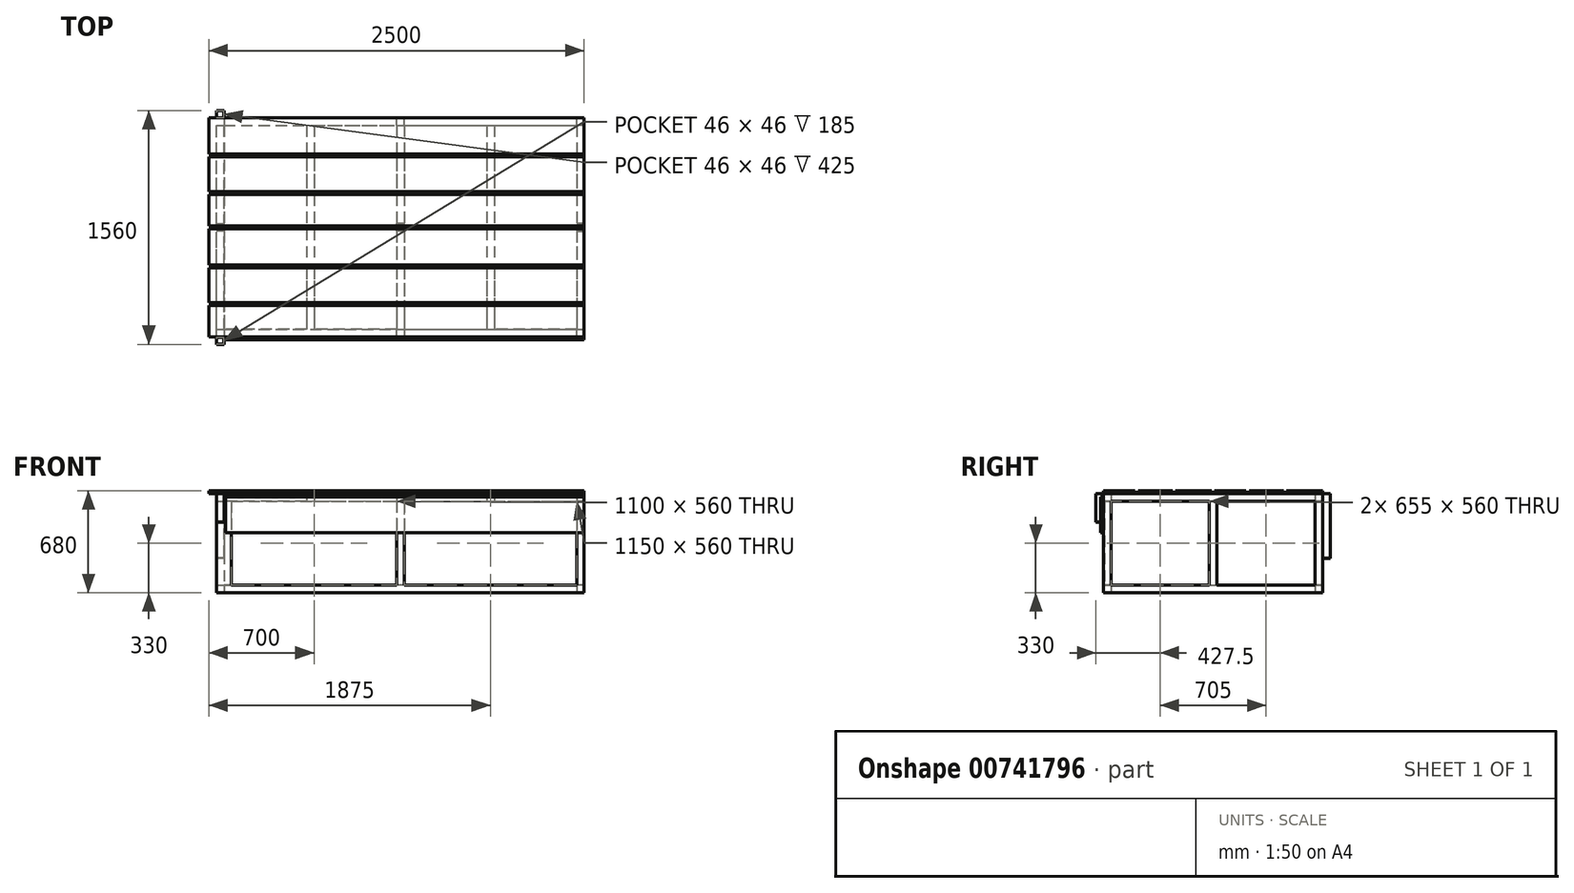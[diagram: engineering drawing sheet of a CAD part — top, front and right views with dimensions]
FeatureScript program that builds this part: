
annotation { "Feature Type Name" : "Feature", "Feature Type Description" : "" }
export const myFeature = defineFeature(function(context is Context, id is Id, definition is map)
    precondition{}
    {
        {
            var Q0;
            Q0=qCreatedBy(makeId("Top.planeOp"),FACE);
            var sketch = newSketch(context, id + "F0", { "sketchPlane" : qUnion([Q0])});
            skLineSegment(sketch, "E0.bottom", {"start": v(1225, -730) * mm, "end": v(-1225, -730) * mm});
            skLineSegment(sketch, "E0.top", {"start": v(1225, 730) * mm, "end": v(-1225, 730) * mm});
            skLineSegment(sketch, "E0.left", {"start": v(1225, -730) * mm, "end": v(1225, 730) * mm});
            skLineSegment(sketch, "E0.right", {"start": v(-1225, -730) * mm, "end": v(-1225, 730) * mm});
            skPoint(sketch, "E0.middle", {"position": v(0, 0) * mm});
            skLineSegment(sketch, "E1.bottom", {"start": v(-1175, 680) * mm, "end": v(1175, 680) * mm});
            skLineSegment(sketch, "E1.top", {"start": v(-1175, -680) * mm, "end": v(1175, -680) * mm});
            skLineSegment(sketch, "E1.left", {"start": v(-1175, 680) * mm, "end": v(-1175, -680) * mm});
            skLineSegment(sketch, "E1.right", {"start": v(1175, 680) * mm, "end": v(1175, -680) * mm});
            skLineSegment(sketch, "E2.bottom", {"start": v(25, 680) * mm, "end": v(-25, 680) * mm});
            skLineSegment(sketch, "E2.top", {"start": v(25, -680) * mm, "end": v(-25, -680) * mm});
            skLineSegment(sketch, "E2.left", {"start": v(25, 680) * mm, "end": v(25, -680) * mm});
            skLineSegment(sketch, "E2.right", {"start": v(-25, 680) * mm, "end": v(-25, -680) * mm});
            skSolve(sketch);
        }
        {
            var Q0;
            Q0 = qSketchRegion(id + "F0", true);
            var Q1;
            Q1=makeQuery(id+"F0.imprint","IMPRINT",FACE,{"disambiguationData":[TD([[makeQuery(id+"F0.imprint","IMPRINT",EDGE,{"derivedFrom":sQuery(id+"F0.wireOp",EDGE,"E2.bottom")}),1.0]])]});
            extrude(context, id + "F1", {"entities" : qUnion([Q0, Q1]), "depth" : 50 * mm, "offsetDistance" : 25 * mm});
        }
        {
            var Q0;
            Q0=makeQuery(id+"F1.opExtrude","CAP_FACE",FACE,{"disambiguationData":[OSD([sQuery(id+"F0.wireOp",EDGE,"E0.bottom"),sQuery(id+"F0.wireOp",EDGE,"E0.top"),sQuery(id+"F0.wireOp",EDGE,"E0.left"),sQuery(id+"F0.wireOp",EDGE,"E0.right"),sQuery(id+"F0.wireOp",EDGE,"E1.bottom"),sQuery(id+"F0.wireOp",EDGE,"E1.top"),sQuery(id+"F0.wireOp",EDGE,"E1.left"),sQuery(id+"F0.wireOp",EDGE,"E1.right"),sQuery(id+"F0.wireOp",EDGE,"E2.left"),sQuery(id+"F0.wireOp",EDGE,"E2.right")])],"isStart":false});
            var sketch = newSketch(context, id + "F2", { "sketchPlane" : qUnion([Q0])});
            skLineSegment(sketch, "E3.bottom", {"start": v(-1225, 730) * mm, "end": v(-1175, 730) * mm});
            skLineSegment(sketch, "E3.top", {"start": v(-1225, 680) * mm, "end": v(-1175, 680) * mm});
            skLineSegment(sketch, "E3.left", {"start": v(-1225, 730) * mm, "end": v(-1225, 680) * mm});
            skLineSegment(sketch, "E3.right", {"start": v(-1175, 730) * mm, "end": v(-1175, 680) * mm});
            skLineSegment(sketch, "E4", {"start": v(-25, 680) * mm, "end": v(-25, 730) * mm});
            skLineSegment(sketch, "E5", {"start": v(25, 680) * mm, "end": v(25, 730) * mm});
            skLineSegment(sketch, "E6", {"start": v(25, 730) * mm, "end": v(-25, 730) * mm});
            skLineSegment(sketch, "E7", {"start": v(-25, 680) * mm, "end": v(25, 680) * mm});
            skLineSegment(sketch, "E8", {"start": v(1175, 680) * mm, "end": v(1175, 730) * mm});
            skLineSegment(sketch, "E9", {"start": v(1175, 730) * mm, "end": v(1225, 730) * mm});
            skLineSegment(sketch, "E10", {"start": v(1225, 730) * mm, "end": v(1225, 680) * mm});
            skLineSegment(sketch, "E11", {"start": v(1225, 680) * mm, "end": v(1175, 680) * mm});
            skLineSegment(sketch, "E12", {"start": v(1175, -680) * mm, "end": v(1225, -680) * mm});
            skLineSegment(sketch, "E13", {"start": v(1225, -680) * mm, "end": v(1225, -730) * mm});
            skLineSegment(sketch, "E14", {"start": v(1225, -730) * mm, "end": v(1175, -730) * mm});
            skLineSegment(sketch, "E15", {"start": v(1175, -730) * mm, "end": v(1175, -680) * mm});
            skLineSegment(sketch, "E16", {"start": v(-25, -680) * mm, "end": v(25, -680) * mm});
            skLineSegment(sketch, "E17", {"start": v(25, -680) * mm, "end": v(25, -730) * mm});
            skLineSegment(sketch, "E18", {"start": v(25, -730) * mm, "end": v(-25, -730) * mm});
            skLineSegment(sketch, "E19", {"start": v(-25, -730) * mm, "end": v(-25, -680) * mm});
            skLineSegment(sketch, "E20", {"start": v(-1175, -680) * mm, "end": v(-1175, -730) * mm});
            skLineSegment(sketch, "E21", {"start": v(-1175, -730) * mm, "end": v(-1225, -730) * mm});
            skLineSegment(sketch, "E22", {"start": v(-1225, -730) * mm, "end": v(-1225, -680) * mm});
            skLineSegment(sketch, "E23", {"start": v(-1225, -680) * mm, "end": v(-1175, -680) * mm});
            skLineSegment(sketch, "E24.bottom", {"start": v(25, -25) * mm, "end": v(-25, -25) * mm});
            skLineSegment(sketch, "E24.top", {"start": v(25, 25) * mm, "end": v(-25, 25) * mm});
            skLineSegment(sketch, "E24.left", {"start": v(25, -25) * mm, "end": v(25, 25) * mm});
            skLineSegment(sketch, "E24.right", {"start": v(-25, -25) * mm, "end": v(-25, 25) * mm});
            skPoint(sketch, "E24.middle", {"position": v(0, 0) * mm});
            skLineSegment(sketch, "E25", {"start": v(0, 0) * mm, "end": v(-1225, 0) * mm});
            skLineSegment(sketch, "E26", {"start": v(-1225, 25) * mm, "end": v(-1175, 25) * mm});
            skLineSegment(sketch, "E27", {"start": v(-1175, 25) * mm, "end": v(-1175, -25) * mm});
            skLineSegment(sketch, "E28", {"start": v(-1175, -25) * mm, "end": v(-1225, -25) * mm});
            skLineSegment(sketch, "E29", {"start": v(-1225, 25) * mm, "end": v(-1225, -25) * mm});
            skLineSegment(sketch, "E30.MirrorCS", {"start": v(1225, 25) * mm, "end": v(1225, -25) * mm});
            skLineSegment(sketch, "E31.MirrorCS", {"start": v(1175, -25) * mm, "end": v(1225, -25) * mm});
            skLineSegment(sketch, "E32.MirrorCS", {"start": v(1225, 25) * mm, "end": v(1175, 25) * mm});
            skLineSegment(sketch, "E33.MirrorCS", {"start": v(1175, 25) * mm, "end": v(1175, -25) * mm});
            skSolve(sketch);
        }
        {
            var Q0;
            Q0 = qSketchRegion(id + "F2", true);
            extrude(context, id + "F3", {"entities" : qUnion([Q0]), "operationType" : NewBodyOperationType.ADD, "depth" : 560 * mm, "offsetDistance" : 25 * mm});
        }
        {
            var Q0;
            Q0=makeQuery(id+"F3.opExtrude","CAP_FACE",FACE,{"disambiguationData":[OSD([sQuery(id+"F2.wireOp",EDGE,"E26"),sQuery(id+"F2.wireOp",EDGE,"E27"),sQuery(id+"F2.wireOp",EDGE,"E28"),sQuery(id+"F2.wireOp",EDGE,"E29")])],"isStart":false});
            var sketch = newSketch(context, id + "F4", { "sketchPlane" : qUnion([Q0])});
            skLineSegment(sketch, "E34", {"start": v(-1225, 25) * mm, "end": v(-1225, 730) * mm});
            skLineSegment(sketch, "E35", {"start": v(-1225, 730) * mm, "end": v(-1175, 730) * mm});
            skLineSegment(sketch, "E36", {"start": v(-1175, 730) * mm, "end": v(1225, 730) * mm});
            skLineSegment(sketch, "E37", {"start": v(1225, 730) * mm, "end": v(1225, -730) * mm});
            skLineSegment(sketch, "E38", {"start": v(1225, -730) * mm, "end": v(-1225, -730) * mm});
            skLineSegment(sketch, "E39", {"start": v(-1225, -730) * mm, "end": v(-1225, 25) * mm});
            skLineSegment(sketch, "E40", {"start": v(-1175, 730) * mm, "end": v(-1175, 680) * mm});
            skLineSegment(sketch, "E41", {"start": v(-1175, 680) * mm, "end": v(-25, 680) * mm});
            skLineSegment(sketch, "E42", {"start": v(-1175, 680) * mm, "end": v(-600, 680) * mm});
            skLineSegment(sketch, "E43", {"start": v(-600, 680) * mm, "end": v(-575, 680) * mm});
            skLineSegment(sketch, "E44", {"start": v(-600, 680) * mm, "end": v(-625, 680) * mm});
            skLineSegment(sketch, "E45", {"start": v(-625, 680) * mm, "end": v(-625, -680) * mm});
            skLineSegment(sketch, "E46.MirrorCS", {"start": v(-575, 680) * mm, "end": v(-575, -680) * mm});
            skLineSegment(sketch, "E47", {"start": v(-25, 680) * mm, "end": v(25, 680) * mm});
            skLineSegment(sketch, "E48", {"start": v(25, 680) * mm, "end": v(1175, 680) * mm});
            skLineSegment(sketch, "E49", {"start": v(25, 680) * mm, "end": v(600, 680) * mm});
            skLineSegment(sketch, "E50", {"start": v(600, 680) * mm, "end": v(575, 680) * mm});
            skLineSegment(sketch, "E51", {"start": v(575, 680) * mm, "end": v(575, -680) * mm});
            skLineSegment(sketch, "E52.MirrorCS", {"start": v(625, 680) * mm, "end": v(625, -680) * mm});
            skLineSegment(sketch, "E53", {"start": v(-25, 680) * mm, "end": v(-25, -680) * mm});
            skLineSegment(sketch, "E54", {"start": v(-25, -680) * mm, "end": v(-575, -680) * mm});
            skLineSegment(sketch, "E55", {"start": v(-625, -680) * mm, "end": v(-1175, -680) * mm});
            skLineSegment(sketch, "E56", {"start": v(-1175, -680) * mm, "end": v(-1175, 680) * mm});
            skLineSegment(sketch, "E57", {"start": v(1175, 680) * mm, "end": v(1175, -680) * mm});
            skLineSegment(sketch, "E58", {"start": v(1175, -680) * mm, "end": v(625, -680) * mm});
            skLineSegment(sketch, "E59", {"start": v(25, 680) * mm, "end": v(25, -680) * mm});
            skLineSegment(sketch, "E60", {"start": v(25, -680) * mm, "end": v(575, -680) * mm});
            skSolve(sketch);
        }
        {
            var Q0;
            Q0 = qSketchRegion(id + "F4", true);
            extrude(context, id + "F5", {"entities" : qUnion([Q0]), "operationType" : NewBodyOperationType.ADD, "depth" : 50 * mm, "offsetDistance" : 25 * mm});
        }
        {
            var Q0;
            {var subQ5=sQuery(id+"F0.wireOp",EDGE,"E1.left");var subQ6=sQuery(id+"F0.wireOp",EDGE,"E1.top");var subQ8=makeQuery(id+"F1.opExtrude","CAP_EDGE",EDGE,{"disambiguationData":[OSD([subQ6]),TDD([makeQuery(id+"F0.imprint","IMPRINT",EDGE,{"disambiguationData":[TD([[makeQuery(id+"F0.imprint","INTERSECT",VERTEX,{"derivedFrom":[subQ6,subQ5]}),-1.0]])],"derivedFrom":subQ6})])],"isStart":false});Q0=makeQuery(id+"F2.imprint","IMPRINT",FACE,{"disambiguationData":[TD([[makeQuery(id+"F2.imprint","IMPRINT",EDGE,{"derivedFrom":subQ8}),1.0]])]});}
            cPlane(context, id + "F6", {"entities" : qUnion([Q0]), "cplaneType" : CPlaneType.OFFSET, "offset" : 420 * mm, "width" : 150 * mm, "height" : 150 * mm});
        }
        {
            var Q0;
            Q0=qCreatedBy(id+"F6.planeOp",FACE);
            var sketch = newSketch(context, id + "F7", { "sketchPlane" : qUnion([Q0])});
            skLineSegment(sketch, "E61.bottom", {"start": v(-1175, -780) * mm, "end": v(-1225, -780) * mm});
            skLineSegment(sketch, "E61.top", {"start": v(-1175, -730) * mm, "end": v(-1225, -730) * mm});
            skLineSegment(sketch, "E61.left", {"start": v(-1175, -780) * mm, "end": v(-1175, -730) * mm});
            skLineSegment(sketch, "E61.right", {"start": v(-1225, -780) * mm, "end": v(-1225, -730) * mm});
            skPoint(sketch, "E61.middle", {"position": v(-1200, -755) * mm});
            skSolve(sketch);
        }
        {
            var Q0;
            Q0 = qSketchRegion(id + "F7", true);
            extrude(context, id + "F8", {"entities" : qUnion([Q0]), "operationType" : NewBodyOperationType.ADD, "depth" : 5 * mm, "offsetDistance" : 25 * mm});
        }
        {
            var Q0;
            Q0=makeQuery(id+"F8.opExtrude","CAP_FACE",FACE,{"disambiguationData":[OSD([sQuery(id+"F7.wireOp",EDGE,"E61.bottom"),sQuery(id+"F7.wireOp",EDGE,"E61.top"),sQuery(id+"F7.wireOp",EDGE,"E61.left"),sQuery(id+"F7.wireOp",EDGE,"E61.right")])],"isStart":false});
            var sketch = newSketch(context, id + "F9", { "sketchPlane" : qUnion([Q0])});
            skLineSegment(sketch, "E62", {"start": v(-1225, -730) * mm, "end": v(-1175, -730) * mm});
            skLineSegment(sketch, "E63", {"start": v(-1175, -730) * mm, "end": v(-1175, -780) * mm});
            skLineSegment(sketch, "E64", {"start": v(-1175, -780) * mm, "end": v(-1225, -780) * mm});
            skLineSegment(sketch, "E65", {"start": v(-1225, -780) * mm, "end": v(-1225, -730) * mm});
            skLineSegment(sketch, "E66.bottom", {"start": v(-1177, -732) * mm, "end": v(-1223, -732) * mm});
            skLineSegment(sketch, "E66.top", {"start": v(-1177, -778) * mm, "end": v(-1223, -778) * mm});
            skLineSegment(sketch, "E66.left", {"start": v(-1177, -732) * mm, "end": v(-1177, -778) * mm});
            skLineSegment(sketch, "E66.right", {"start": v(-1223, -732) * mm, "end": v(-1223, -778) * mm});
            skPoint(sketch, "E66.middle", {"position": v(-1200, -755) * mm});
            skLineSegment(sketch, "E67", {"start": v(-1225, -780) * mm, "end": v(-1223, -780) * mm});
            skLineSegment(sketch, "E68", {"start": v(-1223, -780) * mm, "end": v(-1223, -778) * mm});
            skSolve(sketch);
        }
        {
            var Q0;
            Q0=makeQuery(id+"F9.imprint","IMPRINT",FACE,{"disambiguationData":[TD([[makeQuery(id+"F9.imprint","IMPRINT",EDGE,{"derivedFrom":sQuery(id+"F9.wireOp",EDGE,"E62")}),1.0]])]});
            var Q1;
            Q1=makeQuery(id+"F5.opExtrude","CAP_FACE",FACE,{"disambiguationData":[OSD([sQuery(id+"F4.wireOp",EDGE,"E34"),sQuery(id+"F4.wireOp",EDGE,"E35"),sQuery(id+"F4.wireOp",EDGE,"E36"),sQuery(id+"F4.wireOp",EDGE,"E37"),sQuery(id+"F4.wireOp",EDGE,"E38"),sQuery(id+"F4.wireOp",EDGE,"E39"),sQuery(id+"F4.wireOp",EDGE,"E41"),sQuery(id+"F4.wireOp",EDGE,"E42"),sQuery(id+"F4.wireOp",EDGE,"E45"),sQuery(id+"F4.wireOp",EDGE,"E46.MirrorCS"),sQuery(id+"F4.wireOp",EDGE,"E48"),sQuery(id+"F4.wireOp",EDGE,"E49"),sQuery(id+"F4.wireOp",EDGE,"E51"),sQuery(id+"F4.wireOp",EDGE,"E52.MirrorCS"),sQuery(id+"F4.wireOp",EDGE,"E53"),sQuery(id+"F4.wireOp",EDGE,"E54"),sQuery(id+"F4.wireOp",EDGE,"E55"),sQuery(id+"F4.wireOp",EDGE,"E56"),sQuery(id+"F4.wireOp",EDGE,"E57"),sQuery(id+"F4.wireOp",EDGE,"E58"),sQuery(id+"F4.wireOp",EDGE,"E59"),sQuery(id+"F4.wireOp",EDGE,"E60")])],"isStart":false});
            extrude(context, id + "F10", {"entities" : qUnion([Q0]), "operationType" : NewBodyOperationType.ADD, "endBound" : BoundingType.UP_TO_SURFACE, "depth" : 183.9 * mm, "endBoundEntityFace" : qUnion([Q1]), "offsetDistance" : 25 * mm});
        }
        {
            var Q0;
            {var subQ5=sQuery(id+"F0.wireOp",EDGE,"E1.left");var subQ6=sQuery(id+"F0.wireOp",EDGE,"E1.top");var subQ8=makeQuery(id+"F1.opExtrude","CAP_EDGE",EDGE,{"disambiguationData":[OSD([subQ6]),TDD([makeQuery(id+"F0.imprint","IMPRINT",EDGE,{"disambiguationData":[TD([[makeQuery(id+"F0.imprint","INTERSECT",VERTEX,{"derivedFrom":[subQ6,subQ5]}),-1.0]])],"derivedFrom":subQ6})])],"isStart":false});Q0=makeQuery(id+"F2.imprint","IMPRINT",FACE,{"disambiguationData":[TD([[makeQuery(id+"F2.imprint","IMPRINT",EDGE,{"derivedFrom":subQ8}),1.0]])]});}
            cPlane(context, id + "F11", {"entities" : qUnion([Q0]), "cplaneType" : CPlaneType.OFFSET, "offset" : 180 * mm, "width" : 150 * mm, "height" : 150 * mm});
        }
        {
            var Q0;
            Q0=qCreatedBy(id+"F11.planeOp",FACE);
            var sketch = newSketch(context, id + "F12", { "sketchPlane" : qUnion([Q0])});
            skLineSegment(sketch, "E69.bottom", {"start": v(-1175, 730) * mm, "end": v(-1225, 730) * mm});
            skLineSegment(sketch, "E69.top", {"start": v(-1175, 780) * mm, "end": v(-1225, 780) * mm});
            skLineSegment(sketch, "E69.left", {"start": v(-1175, 730) * mm, "end": v(-1175, 780) * mm});
            skLineSegment(sketch, "E69.right", {"start": v(-1225, 730) * mm, "end": v(-1225, 780) * mm});
            skPoint(sketch, "E69.middle", {"position": v(-1200, 755) * mm});
            skSolve(sketch);
        }
        {
            var Q0;
            Q0 = qSketchRegion(id + "F12", true);
            extrude(context, id + "F13", {"entities" : qUnion([Q0]), "operationType" : NewBodyOperationType.ADD, "depth" : 5 * mm, "offsetDistance" : 25 * mm});
        }
        {
            var Q0;
            Q0=makeQuery(id+"F13.opExtrude","CAP_FACE",FACE,{"disambiguationData":[OSD([sQuery(id+"F12.wireOp",EDGE,"E69.bottom"),sQuery(id+"F12.wireOp",EDGE,"E69.top"),sQuery(id+"F12.wireOp",EDGE,"E69.left"),sQuery(id+"F12.wireOp",EDGE,"E69.right")])],"isStart":false});
            var sketch = newSketch(context, id + "F14", { "sketchPlane" : qUnion([Q0])});
            skLineSegment(sketch, "E70", {"start": v(-1225, 780) * mm, "end": v(-1223, 780) * mm});
            skLineSegment(sketch, "E71", {"start": v(-1223, 780) * mm, "end": v(-1223, 778) * mm});
            skLineSegment(sketch, "E72.bottom", {"start": v(-1223, 778) * mm, "end": v(-1177, 778) * mm});
            skLineSegment(sketch, "E72.top", {"start": v(-1223, 732) * mm, "end": v(-1177, 732) * mm});
            skLineSegment(sketch, "E72.left", {"start": v(-1223, 778) * mm, "end": v(-1223, 732) * mm});
            skLineSegment(sketch, "E72.right", {"start": v(-1177, 778) * mm, "end": v(-1177, 732) * mm});
            skLineSegment(sketch, "E73.bottom", {"start": v(-1225, 780) * mm, "end": v(-1175, 780) * mm});
            skLineSegment(sketch, "E73.top", {"start": v(-1225, 730) * mm, "end": v(-1175, 730) * mm});
            skLineSegment(sketch, "E73.left", {"start": v(-1225, 780) * mm, "end": v(-1225, 730) * mm});
            skLineSegment(sketch, "E73.right", {"start": v(-1175, 780) * mm, "end": v(-1175, 730) * mm});
            skSolve(sketch);
        }
        {
            var Q0;
            Q0=makeQuery(id+"F14.imprint","IMPRINT",FACE,{"disambiguationData":[TD([[makeQuery(id+"F14.imprint","IMPRINT",EDGE,{"derivedFrom":sQuery(id+"F14.wireOp",EDGE,"E72.bottom")}),1.0]])]});
            var Q1;
            {var subQ0=sQuery(id+"F4.wireOp",EDGE,"E60");var subQ1=sQuery(id+"F4.wireOp",EDGE,"E59");var subQ2=sQuery(id+"F4.wireOp",EDGE,"E58");var subQ3=sQuery(id+"F4.wireOp",EDGE,"E57");var subQ4=sQuery(id+"F4.wireOp",EDGE,"E56");var subQ5=sQuery(id+"F4.wireOp",EDGE,"E55");var subQ6=sQuery(id+"F4.wireOp",EDGE,"E54");var subQ7=sQuery(id+"F4.wireOp",EDGE,"E53");var subQ8=sQuery(id+"F4.wireOp",EDGE,"E52.MirrorCS");var subQ9=sQuery(id+"F4.wireOp",EDGE,"E51");var subQ10=sQuery(id+"F4.wireOp",EDGE,"E49");var subQ11=sQuery(id+"F4.wireOp",EDGE,"E48");var subQ12=sQuery(id+"F4.wireOp",EDGE,"E46.MirrorCS");var subQ13=sQuery(id+"F4.wireOp",EDGE,"E45");var subQ14=sQuery(id+"F4.wireOp",EDGE,"E42");var subQ15=sQuery(id+"F4.wireOp",EDGE,"E41");var subQ16=sQuery(id+"F4.wireOp",EDGE,"E39");var subQ17=sQuery(id+"F4.wireOp",EDGE,"E38");var subQ18=sQuery(id+"F4.wireOp",EDGE,"E37");var subQ19=sQuery(id+"F4.wireOp",EDGE,"E36");var subQ20=sQuery(id+"F4.wireOp",EDGE,"E35");var subQ21=sQuery(id+"F4.wireOp",EDGE,"E34");Q1=makeQuery(id+"F10.boolean.opBoolean","MERGE",FACE,{"derivedFrom":[makeQuery(id+"F5.opExtrude","CAP_FACE",FACE,{"disambiguationData":[OSD([subQ21,subQ20,subQ19,subQ18,subQ17,subQ16,subQ15,subQ14,subQ13,subQ12,subQ11,subQ10,subQ9,subQ8,subQ7,subQ6,subQ5,subQ4,subQ3,subQ2,subQ1,subQ0])],"isStart":false}),makeQuery(id+"F10.opExtrude","CAP_FACE",FACE,{"disambiguationData":[OSD([subQ21,subQ20,subQ19,subQ18,subQ17,subQ16,subQ15,subQ14,subQ13,subQ12,subQ11,subQ10,subQ9,subQ8,subQ7,subQ6,subQ5,subQ4,subQ3,subQ2,subQ1,subQ0])],"isStart":false})]});}
            extrude(context, id + "F15", {"entities" : qUnion([Q0]), "operationType" : NewBodyOperationType.ADD, "endBound" : BoundingType.UP_TO_SURFACE, "depth" : 25 * mm, "endBoundEntityFace" : qUnion([Q1]), "offsetDistance" : 25 * mm});
        }
        {
            var Q0;
            Q0=makeQuery(id+"F10.boolean.opBoolean","MERGE",FACE,{"derivedFrom":[makeQuery(id+"F8.boolean.opBoolean","MERGE",FACE,{"derivedFrom":[makeQuery(id+"F3.opExtrude","SWEPT_FACE",FACE,{"disambiguationData":[OSD([sQuery(id+"F2.wireOp",EDGE,"E20")])]}),makeQuery(id+"F8.opExtrude","SWEPT_FACE",FACE,{"disambiguationData":[OSD([sQuery(id+"F7.wireOp",EDGE,"E61.left")])]})]}),makeQuery(id+"F10.opExtrude","SWEPT_FACE",FACE,{"disambiguationData":[OSD([sQuery(id+"F9.wireOp",EDGE,"E63")])]})]});
            var sketch = newSketch(context, id + "F16", { "sketchPlane" : qUnion([Q0])});
            skLineSegment(sketch, "E74.bottom", {"start": v(-730, 610) * mm, "end": v(-725, 610) * mm});
            skLineSegment(sketch, "E74.top", {"start": v(-730, 50) * mm, "end": v(-725, 50) * mm});
            skLineSegment(sketch, "E74.left", {"start": v(-730, 610) * mm, "end": v(-730, 50) * mm});
            skLineSegment(sketch, "E74.right", {"start": v(-725, 610) * mm, "end": v(-725, 50) * mm});
            skLineSegment(sketch, "E75.bottom", {"start": v(730, 610) * mm, "end": v(725, 610) * mm});
            skLineSegment(sketch, "E75.top", {"start": v(730, 50) * mm, "end": v(725, 50) * mm});
            skLineSegment(sketch, "E75.left", {"start": v(730, 610) * mm, "end": v(730, 50) * mm});
            skLineSegment(sketch, "E75.right", {"start": v(725, 610) * mm, "end": v(725, 50) * mm});
            skSolve(sketch);
        }
        {
            var Q0;
            Q0=makeQuery(id+"F16.imprint","IMPRINT",FACE,{"disambiguationData":[TD([[makeQuery(id+"F16.imprint","IMPRINT",EDGE,{"derivedFrom":sQuery(id+"F16.wireOp",EDGE,"E75.bottom")}),1.0]])]});
            var Q1;
            {var subQ3=sQuery(id+"F16.wireOp",EDGE,"E74.bottom");Q1=makeQuery(id+"F16.imprint","IMPRINT",FACE,{"disambiguationData":[TD([[makeQuery(id+"F16.imprint","IMPRINT",EDGE,{"derivedFrom":subQ3}),1.0]])]});}
            extrude(context, id + "F17", {"entities" : qUnion([Q0, Q1]), "operationType" : NewBodyOperationType.ADD, "depth" : 50 * mm, "offsetDistance" : 25 * mm});
        }
        {
            var Q0;
            Q0=makeQuery(id+"F17.boolean.opBoolean","MERGE",FACE,{"derivedFrom":[makeQuery(id+"F5.boolean.opBoolean","MERGE",FACE,{"derivedFrom":[makeQuery(id+"F3.boolean.opBoolean","MERGE",FACE,{"derivedFrom":[makeQuery(id+"F1.opExtrude","SWEPT_FACE",FACE,{"disambiguationData":[OSD([sQuery(id+"F0.wireOp",EDGE,"E0.bottom")])]}),makeQuery(id+"F3.opExtrude","SWEPT_FACE",FACE,{"disambiguationData":[OSD([sQuery(id+"F2.wireOp",EDGE,"E14")])]}),makeQuery(id+"F3.opExtrude","SWEPT_FACE",FACE,{"disambiguationData":[OSD([sQuery(id+"F2.wireOp",EDGE,"E18")])]}),makeQuery(id+"F3.opExtrude","SWEPT_FACE",FACE,{"disambiguationData":[OSD([sQuery(id+"F2.wireOp",EDGE,"E21")])]})]}),makeQuery(id+"F5.opExtrude","SWEPT_FACE",FACE,{"disambiguationData":[OSD([sQuery(id+"F4.wireOp",EDGE,"E38")])]})]}),makeQuery(id+"F17.opExtrude","SWEPT_FACE",FACE,{"disambiguationData":[OSD([sQuery(id+"F16.wireOp",EDGE,"E74.left")])]})]});
            var sketch = newSketch(context, id + "F18", { "sketchPlane" : qUnion([Q0])});
            skLineSegment(sketch, "E76", {"start": v(-1175, 660) * mm, "end": v(-1165, 660) * mm});
            skLineSegment(sketch, "E77", {"start": v(-1165, 660) * mm, "end": v(-1165, 640) * mm});
            skLineSegment(sketch, "E78.bottom", {"start": v(-1165, 640) * mm, "end": v(1225, 640) * mm});
            skLineSegment(sketch, "E78.top", {"start": v(-1165, 400) * mm, "end": v(1225, 400) * mm});
            skLineSegment(sketch, "E78.left", {"start": v(-1165, 640) * mm, "end": v(-1165, 400) * mm});
            skLineSegment(sketch, "E78.right", {"start": v(1225, 640) * mm, "end": v(1225, 400) * mm});
            skSolve(sketch);
        }
        {
            var Q0;
            Q0 = qSketchRegion(id + "F18", true);
            extrude(context, id + "F19", {"entities" : qUnion([Q0]), "depth" : 20 * mm, "offsetDistance" : 25 * mm});
        }
        {
            var Q0;
            {var subQ0=sQuery(id+"F4.wireOp",EDGE,"E60");var subQ1=sQuery(id+"F4.wireOp",EDGE,"E59");var subQ2=sQuery(id+"F4.wireOp",EDGE,"E58");var subQ3=sQuery(id+"F4.wireOp",EDGE,"E57");var subQ4=sQuery(id+"F4.wireOp",EDGE,"E56");var subQ5=sQuery(id+"F4.wireOp",EDGE,"E55");var subQ6=sQuery(id+"F4.wireOp",EDGE,"E54");var subQ7=sQuery(id+"F4.wireOp",EDGE,"E53");var subQ8=sQuery(id+"F4.wireOp",EDGE,"E52.MirrorCS");var subQ9=sQuery(id+"F4.wireOp",EDGE,"E51");var subQ10=sQuery(id+"F4.wireOp",EDGE,"E49");var subQ11=sQuery(id+"F4.wireOp",EDGE,"E48");var subQ12=sQuery(id+"F4.wireOp",EDGE,"E46.MirrorCS");var subQ13=sQuery(id+"F4.wireOp",EDGE,"E45");var subQ14=sQuery(id+"F4.wireOp",EDGE,"E42");var subQ15=sQuery(id+"F4.wireOp",EDGE,"E41");var subQ16=sQuery(id+"F4.wireOp",EDGE,"E39");var subQ17=sQuery(id+"F4.wireOp",EDGE,"E38");var subQ18=sQuery(id+"F4.wireOp",EDGE,"E37");var subQ19=sQuery(id+"F4.wireOp",EDGE,"E36");var subQ20=sQuery(id+"F4.wireOp",EDGE,"E35");var subQ21=sQuery(id+"F4.wireOp",EDGE,"E34");Q0=makeQuery(id+"F15.boolean.opBoolean","MERGE",FACE,{"derivedFrom":[makeQuery(id+"F10.boolean.opBoolean","MERGE",FACE,{"derivedFrom":[makeQuery(id+"F5.opExtrude","CAP_FACE",FACE,{"disambiguationData":[OSD([subQ21,subQ20,subQ19,subQ18,subQ17,subQ16,subQ15,subQ14,subQ13,subQ12,subQ11,subQ10,subQ9,subQ8,subQ7,subQ6,subQ5,subQ4,subQ3,subQ2,subQ1,subQ0])],"isStart":false}),makeQuery(id+"F10.opExtrude","CAP_FACE",FACE,{"disambiguationData":[OSD([subQ21,subQ20,subQ19,subQ18,subQ17,subQ16,subQ15,subQ14,subQ13,subQ12,subQ11,subQ10,subQ9,subQ8,subQ7,subQ6,subQ5,subQ4,subQ3,subQ2,subQ1,subQ0])],"isStart":false})]}),makeQuery(id+"F15.opExtrude","CAP_FACE",FACE,{"disambiguationData":[OSD([subQ21,subQ20,subQ19,subQ18,subQ17,subQ16,subQ15,subQ14,subQ13,subQ12,subQ11,subQ10,subQ9,subQ8,subQ7,subQ6,subQ5,subQ4,subQ3,subQ2,subQ1,subQ0])],"isStart":false})]});}
            var sketch = newSketch(context, id + "F20", { "sketchPlane" : qUnion([Q0])});
            skLineSegment(sketch, "E79.bottom", {"start": v(1225, 730) * mm, "end": v(-1275, 730) * mm});
            skLineSegment(sketch, "E79.top", {"start": v(1225, -730) * mm, "end": v(-1275, -730) * mm});
            skLineSegment(sketch, "E79.left", {"start": v(1225, 730) * mm, "end": v(1225, -730) * mm});
            skLineSegment(sketch, "E79.right", {"start": v(-1275, 730) * mm, "end": v(-1275, -730) * mm});
            skLineSegment(sketch, "E80", {"start": v(-1225, 730) * mm, "end": v(-1275, 730) * mm});
            skLineSegment(sketch, "E81.bottom", {"start": v(-1165, -730) * mm, "end": v(1225, -730) * mm});
            skLineSegment(sketch, "E81.top", {"start": v(-1165, -750) * mm, "end": v(1225, -750) * mm});
            skLineSegment(sketch, "E81.left", {"start": v(-1165, -730) * mm, "end": v(-1165, -750) * mm});
            skLineSegment(sketch, "E81.right", {"start": v(1225, -730) * mm, "end": v(1225, -750) * mm});
            skSolve(sketch);
        }
        {
            var Q0;
            {var subQ0=sQuery(id+"F20.wireOp",EDGE,"E79.right");Q0=makeQuery(id+"F20.imprint","IMPRINT",FACE,{"disambiguationData":[TD([[makeQuery(id+"F20.imprint","IMPRINT",EDGE,{"derivedFrom":subQ0}),1.0]])]});}
            var Q1;
            {var subQ3=sQuery(id+"F20.wireOp",EDGE,"E79.left");Q1=makeQuery(id+"F20.imprint","IMPRINT",FACE,{"disambiguationData":[TD([[makeQuery(id+"F20.imprint","IMPRINT",EDGE,{"derivedFrom":subQ3}),-1.0]])]});}
            var Q2;
            Q2=makeQuery(id+"F20.imprint","IMPRINT",FACE,{"disambiguationData":[TD([[makeQuery(id+"F20.imprint","IMPRINT",EDGE,{"derivedFrom":makeQuery(id+"F5.opExtrude","CAP_EDGE",EDGE,{"disambiguationData":[OSD([sQuery(id+"F4.wireOp",EDGE,"E42")])],"isStart":false})}),-1.0]])]});
            var Q3;
            Q3=makeQuery(id+"F20.imprint","IMPRINT",FACE,{"disambiguationData":[TD([[makeQuery(id+"F20.imprint","IMPRINT",EDGE,{"derivedFrom":makeQuery(id+"F5.opExtrude","CAP_EDGE",EDGE,{"disambiguationData":[OSD([sQuery(id+"F4.wireOp",EDGE,"E41")])],"isStart":false})}),-1.0]])]});
            var Q4;
            Q4=makeQuery(id+"F20.imprint","IMPRINT",FACE,{"disambiguationData":[TD([[makeQuery(id+"F20.imprint","IMPRINT",EDGE,{"derivedFrom":makeQuery(id+"F5.opExtrude","CAP_EDGE",EDGE,{"disambiguationData":[OSD([sQuery(id+"F4.wireOp",EDGE,"E49")])],"isStart":false})}),-1.0]])]});
            var Q5;
            Q5=makeQuery(id+"F20.imprint","IMPRINT",FACE,{"disambiguationData":[TD([[makeQuery(id+"F20.imprint","IMPRINT",EDGE,{"derivedFrom":makeQuery(id+"F5.opExtrude","CAP_EDGE",EDGE,{"disambiguationData":[OSD([sQuery(id+"F4.wireOp",EDGE,"E48")])],"isStart":false})}),-1.0]])]});
            var Q6;
            Q6=makeQuery(id+"F20.imprint","IMPRINT",FACE,{"disambiguationData":[TD([[makeQuery(id+"F20.imprint","IMPRINT",EDGE,{"derivedFrom":sQuery(id+"F20.wireOp",EDGE,"E81.bottom")}),1.0]])]});
            extrude(context, id + "F21", {"entities" : qUnion([Q0, Q1, Q2, Q3, Q4, Q5, Q6]), "depth" : 20 * mm, "offsetDistance" : 25 * mm});
        }
        {
            var Q0;
            Q0=makeQuery(id+"F21.opExtrude","SWEPT_FACE",FACE,{"disambiguationData":[OSD([sQuery(id+"F20.wireOp",EDGE,"E79.right")])]});
            var sketch = newSketch(context, id + "F22", { "sketchPlane" : qUnion([Q0])});
            skSolve(sketch);
        }
        {
            var Q0;
            {var subQ0=sQuery(id+"F20.wireOp",EDGE,"E79.right");Q0=makeQuery(id+"F22.imprint","IMPRINT",FACE,{"disambiguationData":[TD([[makeQuery(id+"F22.imprint","IMPRINT",EDGE,{"derivedFrom":makeQuery(id+"F21.opExtrude","CAP_EDGE",EDGE,{"disambiguationData":[OSD([subQ0])],"isStart":true})}),1.0]])]});}
            var sketch = newSketch(context, id + "F23", { "sketchPlane" : qUnion([Q0])});
            skLineSegment(sketch, "E82", {"start": v(730, 680) * mm, "end": v(10, 680) * mm});
            skLineSegment(sketch, "E83.bottom", {"start": v(10, 680) * mm, "end": v(-10, 680) * mm});
            skLineSegment(sketch, "E83.top", {"start": v(10, 660) * mm, "end": v(-10, 660) * mm});
            skLineSegment(sketch, "E83.left", {"start": v(10, 680) * mm, "end": v(10, 660) * mm});
            skLineSegment(sketch, "E83.right", {"start": v(-10, 680) * mm, "end": v(-10, 660) * mm});
            skLineSegment(sketch, "E84", {"start": v(-10, 680) * mm, "end": v(-133.71, 680) * mm});
            skLineSegment(sketch, "E85", {"start": v(730, 680) * mm, "end": v(520, 680) * mm});
            skLineSegment(sketch, "E86.bottom", {"start": v(520, 680) * mm, "end": v(500, 680) * mm});
            skLineSegment(sketch, "E86.top", {"start": v(520, 660) * mm, "end": v(500, 660) * mm});
            skLineSegment(sketch, "E86.left", {"start": v(520, 680) * mm, "end": v(520, 660) * mm});
            skLineSegment(sketch, "E86.right", {"start": v(500, 680) * mm, "end": v(500, 660) * mm});
            skLineSegment(sketch, "E87", {"start": v(500, 680) * mm, "end": v(270, 680) * mm});
            skLineSegment(sketch, "E88.bottom", {"start": v(270, 680) * mm, "end": v(250, 680) * mm});
            skLineSegment(sketch, "E88.top", {"start": v(270, 660) * mm, "end": v(250, 660) * mm});
            skLineSegment(sketch, "E88.left", {"start": v(270, 680) * mm, "end": v(270, 660) * mm});
            skLineSegment(sketch, "E88.right", {"start": v(250, 680) * mm, "end": v(250, 660) * mm});
            skLineSegment(sketch, "E89", {"start": v(-10, 680) * mm, "end": v(-220, 680) * mm});
            skLineSegment(sketch, "E90.bottom", {"start": v(-220, 680) * mm, "end": v(-240, 680) * mm});
            skLineSegment(sketch, "E90.top", {"start": v(-220, 660) * mm, "end": v(-240, 660) * mm});
            skLineSegment(sketch, "E90.left", {"start": v(-220, 680) * mm, "end": v(-220, 660) * mm});
            skLineSegment(sketch, "E90.right", {"start": v(-240, 680) * mm, "end": v(-240, 660) * mm});
            skLineSegment(sketch, "E91", {"start": v(-240, 680) * mm, "end": v(-470, 680) * mm});
            skLineSegment(sketch, "E92.bottom", {"start": v(-470, 680) * mm, "end": v(-490, 680) * mm});
            skLineSegment(sketch, "E92.top", {"start": v(-470, 660) * mm, "end": v(-490, 660) * mm});
            skLineSegment(sketch, "E92.left", {"start": v(-470, 680) * mm, "end": v(-470, 660) * mm});
            skLineSegment(sketch, "E92.right", {"start": v(-490, 680) * mm, "end": v(-490, 660) * mm});
            skSolve(sketch);
        }
        {
            var Q0;
            Q0 = qSketchRegion(id + "F23", true);
            var Q1;
            Q1=makeQuery(id+"F21.opExtrude","SWEPT_FACE",FACE,{"disambiguationData":[OSD([sQuery(id+"F20.wireOp",EDGE,"E79.left"),sQuery(id+"F20.wireOp",EDGE,"E81.right")])]});
            extrude(context, id + "F24", {"entities" : qUnion([Q0]), "operationType" : NewBodyOperationType.REMOVE, "endBound" : BoundingType.UP_TO_SURFACE, "oppositeDirection" : true, "depth" : 25 * mm, "endBoundEntityFace" : qUnion([Q1]), "offsetDistance" : 25 * mm});
        }
    });
